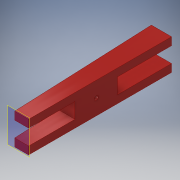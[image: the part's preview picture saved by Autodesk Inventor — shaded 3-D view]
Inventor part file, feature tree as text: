
AUTODESK INVENTOR PART (.ipt)
format: ipt  version: 2019.1 (Build 231200000, 200)  size: 166,400 bytes
history: native  units: in
note: dims shown in document units (in); Inventor stores cm internally (conversion verified against a paired STEP export)
features: sketch x5, extrude x4, plane x2, hole x1, split x1
ambient origin geometry x8: Origin, YZ Plane, XZ Plane, XY Plane, X Axis, Y Axis, Z Axis, Center Point
bodies: Solid1 (feature_tree)
feature tree (13):
  extrude  "Extrusion1"  Depth=18.5in
  plane  "Work Plane1"
  extrude  "Extrusion2"  TaperAngle=0.0deg  [1 undecoded]
  hole  "Hole2"  [1 undecoded]
  extrude  "Extrusion3"  Depth=3.5in
  plane  "Work Plane2"
  split  "Split2"
  extrude  "Extrusion4"  Depth=0.4375in
  sketch  "Sketch1"  dims[d0=18.5in d1=0.0172in]
  sketch  "Sketch2"  dims[d2=2.0in d3=0.0in]
  sketch  "Sketch4"  dims[d4=0.5in d5=0.0in]
  sketch  "Sketch6"  dims[d16=1.0in d17=3.5in]
  sketch  "Sketch7"  dims[d18=13.625in d19=0.266in d20=0.75in d21=0.7in d22=1.65in d23=0.5635in d24=1.0in d25=0.8108in d26=0.4375in d27=0.92in d28=0.0in d29=-9.25in d30=1.0in d31=7.0in d32=6.0in d33=1.0in d34=0.0in]
note: 2 required parameter values undecoded (feature->parameter linkage not recoverable at this tier; creation-order binding heuristic only, values carry confidence <= 0.55)
